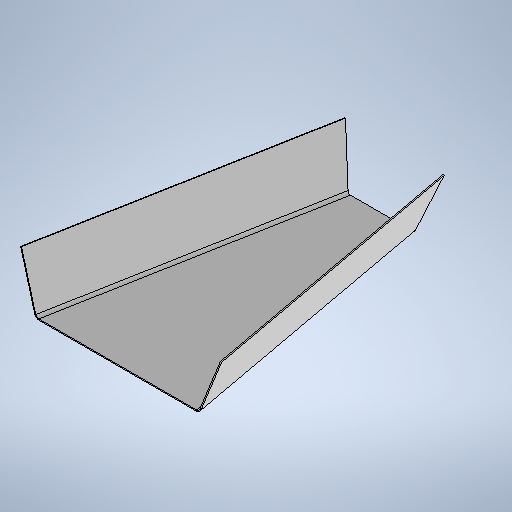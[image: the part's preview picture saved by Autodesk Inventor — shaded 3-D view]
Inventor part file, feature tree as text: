
AUTODESK INVENTOR PART (.ipt)
format: ipt  version: 2025.3 (Build 293356030, 356C)  size: 316,928 bytes
history: native  units: mm
features: sheet_metal_op x4, sketch x3, other x3, extrude x1
ambient origin geometry x8: Origin, YZ Plane, XZ Plane, XY Plane, X Axis, Y Axis, Z Axis, Center Point
bodies: Body1 (feature_tree)
feature tree (11):
  sheet_metal_op  "Face3"
  sheet_metal_op  "Flange1"
  extrude  "Extrusion2"  Depth=500.0mm
  sketch  "Sketch6"  dims[d33=115.0mm d34=500.0mm]
  other  "Plate3"
  sketch  "Sketch7"  dims[d35=300.0mm]
  other  "Plate4"
  sheet_metal_op  "Bend1"
  sheet_metal_op  "Corner1"
  sketch  "Sketch8"  dims[d36=2.0mm d37=2.0mm d38=1.0mm d39=4.0mm d40=6.0mm d41=100.0mm d42=12.217305mm d43=6.0mm d44=8.0mm d45=2.0mm d46=6.0mm d47=15.0deg d48=0.0mm d49=0.0mm]
  other  "Definition1"
